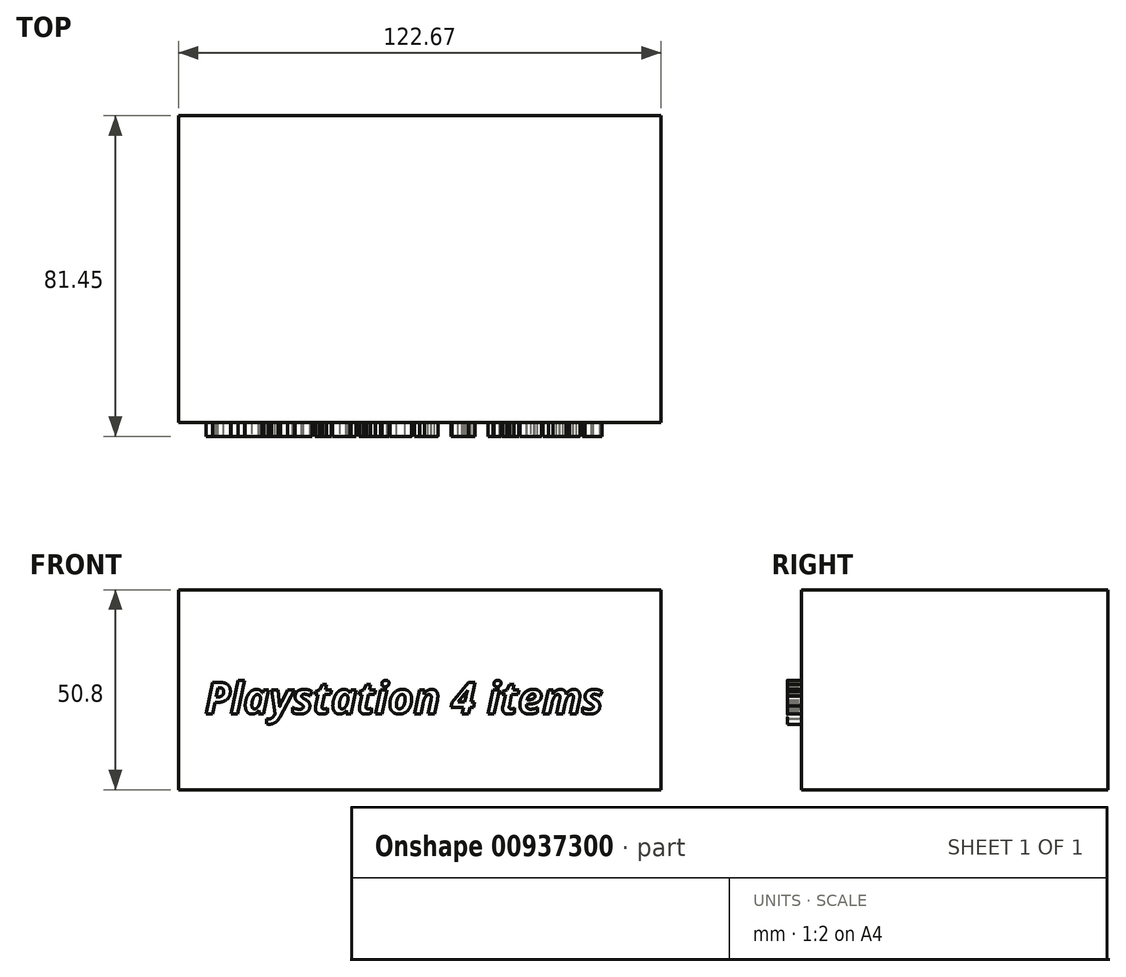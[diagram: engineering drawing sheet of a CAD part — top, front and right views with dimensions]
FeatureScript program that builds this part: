
annotation { "Feature Type Name" : "Feature", "Feature Type Description" : "" }
export const myFeature = defineFeature(function(context is Context, id is Id, definition is map)
    precondition{}
    {
        {
            var Q0;
            Q0=qCreatedBy(makeId("Top.planeOp"),FACE);
            var sketch = newSketch(context, id + "F0", { "sketchPlane" : qUnion([Q0])});
            skLineSegment(sketch, "E0.bottom", {"start": v(-64.05, 39.54) * mm, "end": v(58.62, 39.54) * mm});
            skLineSegment(sketch, "E0.top", {"start": v(-64.05, -38.35) * mm, "end": v(58.62, -38.35) * mm});
            skLineSegment(sketch, "E0.left", {"start": v(-64.05, 39.54) * mm, "end": v(-64.05, -38.35) * mm});
            skLineSegment(sketch, "E0.right", {"start": v(58.62, 39.54) * mm, "end": v(58.62, -38.35) * mm});
            skSolve(sketch);
        }
        {
            var Q0;
            Q0=makeQuery(id+"F0.imprint","IMPRINT",FACE,{"disambiguationData":[TD([[makeQuery(id+"F0.imprint","IMPRINT",EDGE,{"derivedFrom":sQuery(id+"F0.wireOp",EDGE,"E0.bottom")}),-1.0]])]});
            extrude(context, id + "F1", {"entities" : qUnion([Q0]), "depth" : 50.8 * mm, "offsetDistance" : 25.4 * mm});
        }
        {
            var Q0;
            Q0=qCreatedBy(makeId("Front.planeOp"),FACE);
            var sketch = newSketch(context, id + "F2", { "sketchPlane" : qUnion([Q0])});
            skText(sketch, "E1", { "text": "Playstation 4 items\n", "fontName": "OpenSans-BoldItalic.ttf"});
            const initialGuessF2  = {"E1": [-0.05732, 0.01933, 1, 0, 0.00802]};
            skSetInitialGuess(sketch, initialGuessF2);
            skSolve(sketch);
        }
        {
            var Q0;
            Q0 = qSketchRegion(id + "F2", true);
            extrude(context, id + "F3", {"entities" : qUnion([Q0]), "operationType" : NewBodyOperationType.ADD, "depth" : 41.9 * mm, "offsetDistance" : 25.4 * mm});
        }
    });
